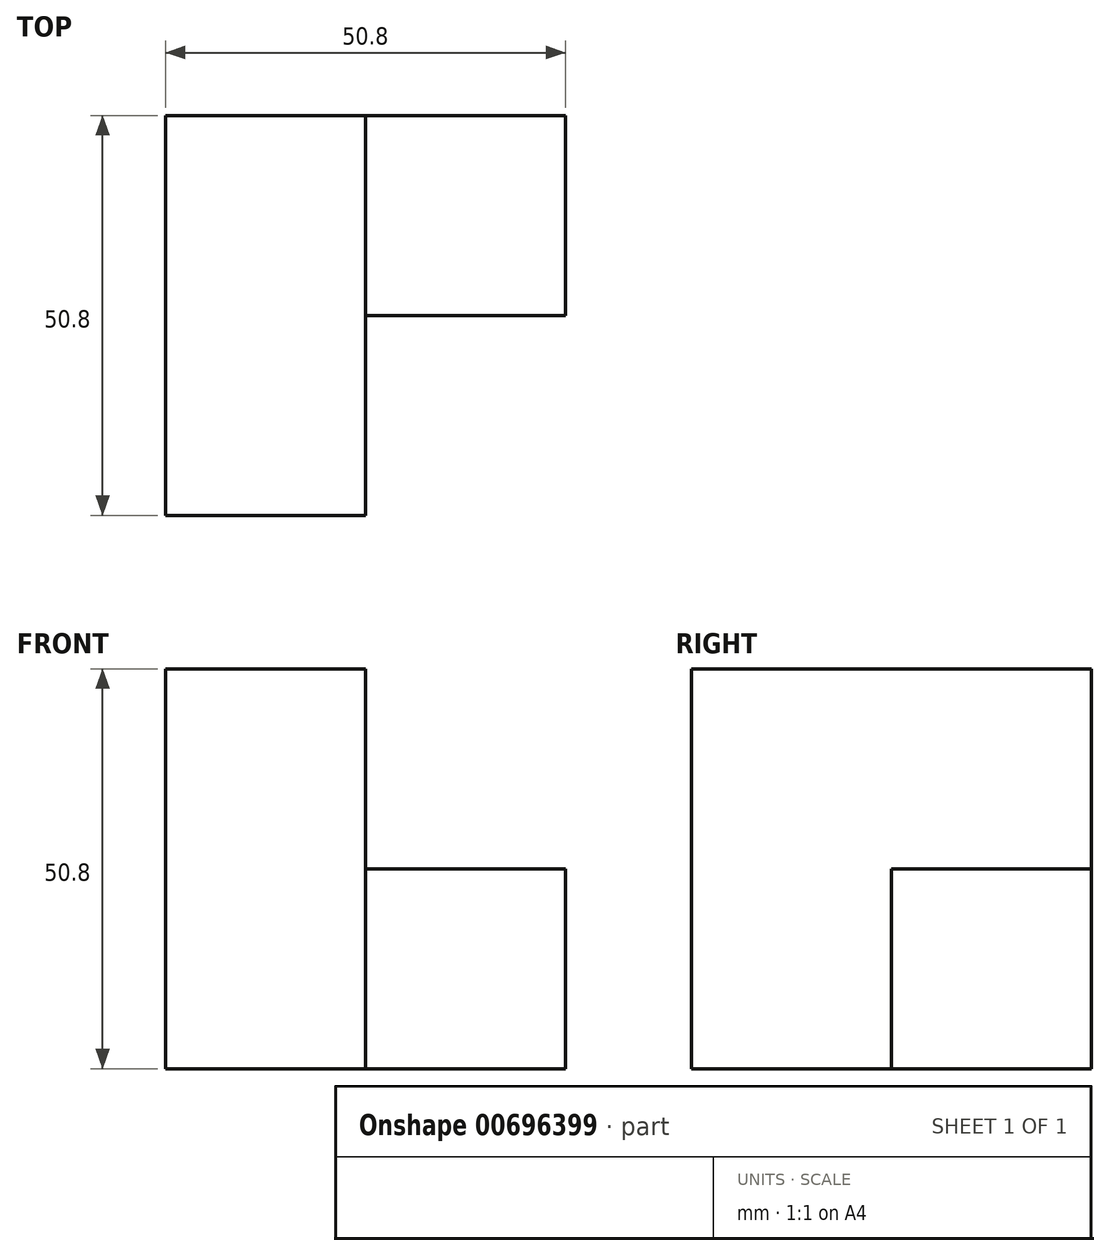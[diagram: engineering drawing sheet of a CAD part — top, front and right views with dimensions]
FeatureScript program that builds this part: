
annotation { "Feature Type Name" : "Feature", "Feature Type Description" : "" }
export const myFeature = defineFeature(function(context is Context, id is Id, definition is map)
    precondition{}
    {
        {
            var Q0;
            Q0=qCreatedBy(makeId("Front.planeOp"),FACE);
            var sketch = newSketch(context, id + "F0", { "sketchPlane" : qUnion([Q0])});
            skLineSegment(sketch, "E0", {"start": v(0, 0) * mm, "end": v(0, 50.8) * mm});
            skLineSegment(sketch, "E1", {"start": v(0, 0) * mm, "end": v(-25.4, 0) * mm});
            skLineSegment(sketch, "E2", {"start": v(0, 50.8) * mm, "end": v(-25.4, 50.8) * mm});
            skLineSegment(sketch, "E3", {"start": v(-25.4, 50.8) * mm, "end": v(-25.4, 0) * mm});
            skLineSegment(sketch, "E4", {"start": v(-25.4, 0) * mm, "end": v(-50.8, 0) * mm});
            skLineSegment(sketch, "E5", {"start": v(-50.8, 0) * mm, "end": v(-50.8, 25.4) * mm});
            skLineSegment(sketch, "E6", {"start": v(-50.8, 25.4) * mm, "end": v(-25.4, 25.4) * mm});
            skSolve(sketch);
        }
        {
            var Q0;
            Q0=makeQuery(id+"F0.imprint","IMPRINT",FACE,{"disambiguationData":[TD([[makeQuery(id+"F0.imprint","IMPRINT",EDGE,{"derivedFrom":sQuery(id+"F0.wireOp",EDGE,"E0")}),1.0]])]});
            extrude(context, id + "F1", {"entities" : qUnion([Q0]), "depth" : 50.8 * mm, "offsetDistance" : 25.4 * mm});
        }
        {
            var Q0;
            Q0=qCreatedBy(makeId("Front.planeOp"),FACE);
            var sketch = newSketch(context, id + "F2", { "sketchPlane" : qUnion([Q0])});
            skLineSegment(sketch, "E7.bottom", {"start": v(0, 0) * mm, "end": v(25.4, 0) * mm});
            skLineSegment(sketch, "E7.top", {"start": v(0, 25.4) * mm, "end": v(25.4, 25.4) * mm});
            skLineSegment(sketch, "E7.left", {"start": v(0, 0) * mm, "end": v(0, 25.4) * mm});
            skLineSegment(sketch, "E7.right", {"start": v(25.4, 0) * mm, "end": v(25.4, 25.4) * mm});
            skSolve(sketch);
        }
        {
            var Q0;
            Q0=makeQuery(id+"F2.imprint","IMPRINT",FACE,{"disambiguationData":[TD([[makeQuery(id+"F2.imprint","IMPRINT",EDGE,{"derivedFrom":sQuery(id+"F2.wireOp",EDGE,"E7.bottom")}),1.0]])]});
            extrude(context, id + "F3", {"entities" : qUnion([Q0]), "operationType" : NewBodyOperationType.ADD, "depth" : 25.4 * mm, "offsetDistance" : 25.4 * mm});
        }
    });
